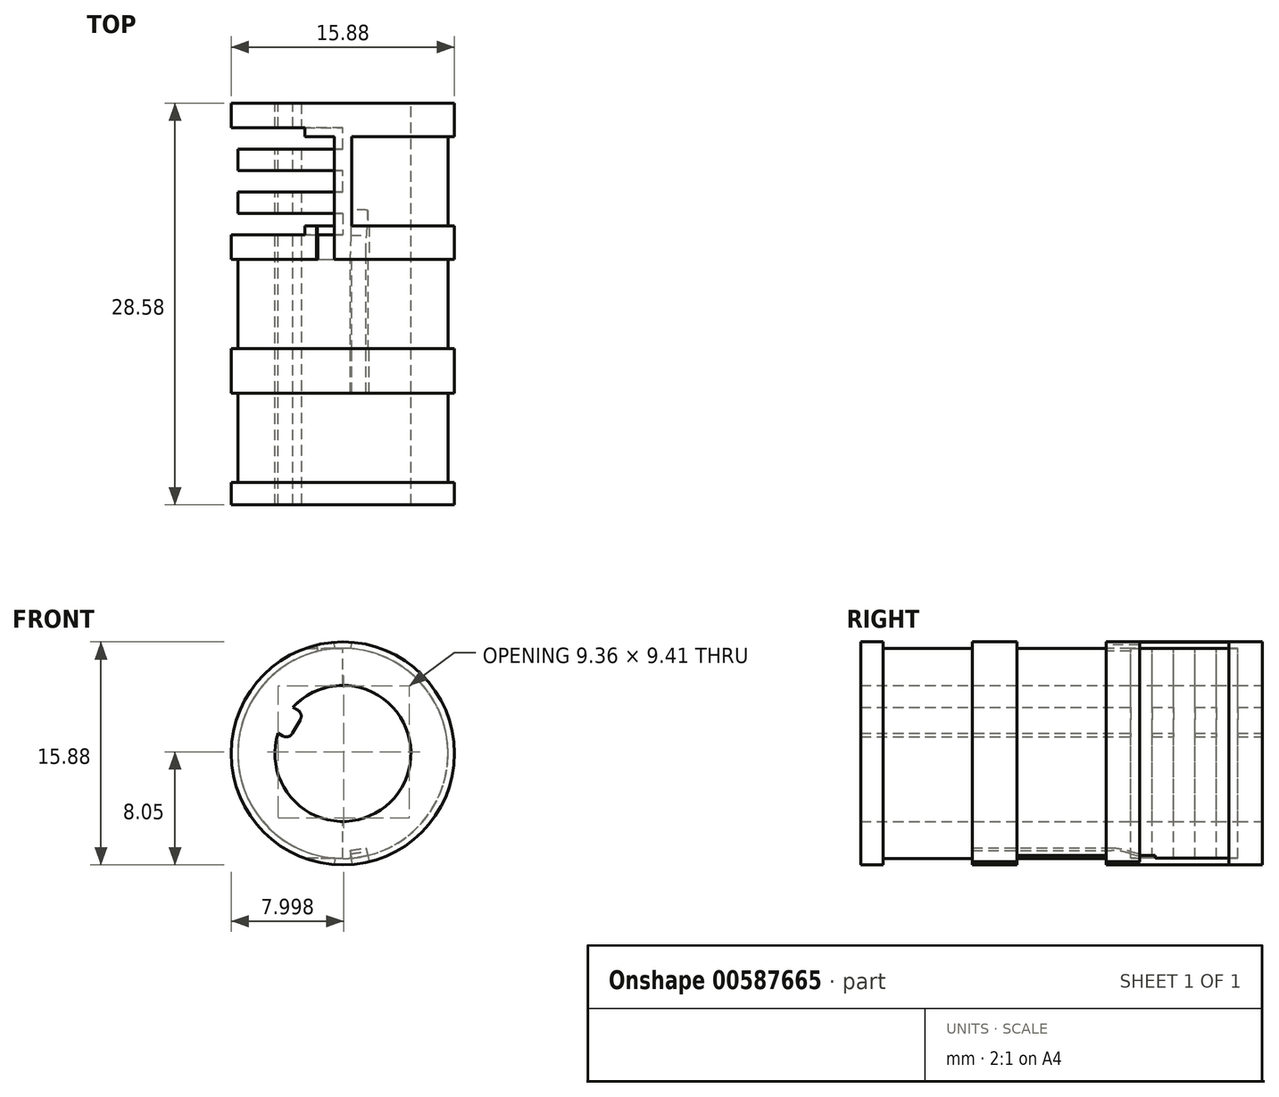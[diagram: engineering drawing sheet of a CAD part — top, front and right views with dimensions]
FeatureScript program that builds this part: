
annotation { "Feature Type Name" : "Feature", "Feature Type Description" : "" }
export const myFeature = defineFeature(function(context is Context, id is Id, definition is map)
    precondition{}
    {
        {
            var Q0;
            Q0=qCreatedBy(makeId("Front.planeOp"),FACE);
            var sketch = newSketch(context, id + "F0", { "sketchPlane" : qUnion([Q0])});
            skCircle(sketch, "E0", {"center": v(0, 0) * mm, "radius": 7.94 * mm});
            skCircle(sketch, "E1", {"center": v(0, 0) * mm, "radius": 4.84 * mm});
            skSolve(sketch);
        }
        {
            var Q0;
            Q0 = qSketchRegion(id + "F0", true);
            extrude(context, id + "F1", {"entities" : qUnion([Q0]), "endBound" : BoundingType.SYMMETRIC, "depth" : 11.1 * mm, "offsetDistance" : 25.4 * mm});
        }
        {
            var Q0;
            Q0=qCreatedBy(makeId("Front.planeOp"),FACE);
            var sketch = newSketch(context, id + "F2", { "sketchPlane" : qUnion([Q0])});
            skCircle(sketch, "E2.0", {"center": v(0, 0) * mm, "radius": 7.94 * mm, "construction": true});
            skLineSegment(sketch, "E3", {"start": v(0, 0) * mm, "end": v(0, 7.94) * mm, "construction": true});
            skLineSegment(sketch, "E4", {"start": v(0, 0) * mm, "end": v(0, -7.94) * mm, "construction": true});
            skLineSegment(sketch, "E5", {"start": v(0, 0) * mm, "end": v(-0.62, 7.91) * mm});
            skLineSegment(sketch, "E6", {"start": v(0, 0) * mm, "end": v(0.62, 7.91) * mm});
            skLineSegment(sketch, "E7", {"start": v(-0.62, 7.91) * mm, "end": v(0.62, 7.91) * mm, "construction": true});
            skLineSegment(sketch, "E8", {"start": v(0, 0) * mm, "end": v(0.62, -7.91) * mm});
            skLineSegment(sketch, "E9", {"start": v(0, 0) * mm, "end": v(-0.62, -7.91) * mm});
            skCircle(sketch, "E10", {"center": v(0, 0) * mm, "radius": 7.48 * mm});
            skCircle(sketch, "E11", {"center": v(0, 0) * mm, "radius": 8.45 * mm});
            skLineSegment(sketch, "E12", {"start": v(-0.62, 7.91) * mm, "end": v(-0.66, 8.42) * mm});
            skLineSegment(sketch, "E13", {"start": v(0.62, 7.91) * mm, "end": v(0.66, 8.42) * mm});
            skLineSegment(sketch, "E14", {"start": v(0.62, -7.91) * mm, "end": v(0.66, -8.42) * mm});
            skLineSegment(sketch, "E15", {"start": v(-0.62, -7.91) * mm, "end": v(-0.66, -8.42) * mm});
            skSolve(sketch);
        }
        {
            var Q0;
            {var subQ5=sQuery(id+"F2.wireOp",EDGE,"E13");Q0=makeQuery(id+"F2.imprint","IMPRINT",FACE,{"disambiguationData":[TD([[makeQuery(id+"F2.imprint","IMPRINT",EDGE,{"derivedFrom":subQ5}),-1.0]])]});}
            var Q1;
            {var subQ0=sQuery(id+"F2.wireOp",EDGE,"E12");Q1=makeQuery(id+"F2.imprint","IMPRINT",FACE,{"disambiguationData":[TD([[makeQuery(id+"F2.imprint","IMPRINT",EDGE,{"derivedFrom":subQ0}),1.0]])]});}
            extrude(context, id + "F3", {"entities" : qUnion([Q0, Q1]), "operationType" : NewBodyOperationType.REMOVE, "endBound" : BoundingType.SYMMETRIC, "oppositeDirection" : true, "depth" : 6.35 * mm, "offsetDistance" : 25.4 * mm});
        }
        {
            var Q0;
            Q0=qCreatedBy(makeId("Front.planeOp"),FACE);
            var sketch = newSketch(context, id + "F4", { "sketchPlane" : qUnion([Q0])});
            skLineSegment(sketch, "E16", {"start": v(0, 0) * mm, "end": v(-4.2, 2.42) * mm, "construction": true});
            skArc(sketch, "E17.0", {"start": v(-3.55, 3.28) * mm, "mid": v(-4.2, 2.42) * mm, "end": v(-4.62, 1.44) * mm});
            skLineSegment(sketch, "E18", {"start": v(-3.31, 1.91) * mm, "end": v(-3.84, 0.99) * mm});
            skLineSegment(sketch, "E19", {"start": v(-3.31, 1.91) * mm, "end": v(-2.78, 2.84) * mm});
            skLineSegment(sketch, "E20", {"start": v(-2.78, 2.84) * mm, "end": v(-3.55, 3.28) * mm});
            skLineSegment(sketch, "E21", {"start": v(-3.84, 0.99) * mm, "end": v(-4.62, 1.44) * mm});
            skLineSegment(sketch, "E22", {"start": v(0, 0) * mm, "end": v(0, -4.84) * mm, "construction": true});
            skSolve(sketch);
        }
        {
            var Q0;
            Q0=makeQuery(id+"F4.imprint","IMPRINT",FACE,{"disambiguationData":[TD([[makeQuery(id+"F4.imprint","IMPRINT",EDGE,{"derivedFrom":sQuery(id+"F4.wireOp",EDGE,"E17.0")}),1.0]])]});
            extrude(context, id + "F5", {"entities" : qUnion([Q0]), "operationType" : NewBodyOperationType.ADD, "endBound" : BoundingType.SYMMETRIC, "depth" : 11.1 * mm, "offsetDistance" : 25.4 * mm});
        }
        {
            var Q0;
            Q0=makeQuery(id+"F5.opExtrude","SWEPT_EDGE",EDGE,{"disambiguationData":[OSD([sQuery(id+"F4.wireOp",EDGE,"E19"),sQuery(id+"F4.wireOp",EDGE,"E20")])]});
            var Q1;
            Q1=makeQuery(id+"F5.opExtrude","SWEPT_EDGE",EDGE,{"disambiguationData":[OSD([sQuery(id+"F4.wireOp",EDGE,"E18"),sQuery(id+"F4.wireOp",EDGE,"E21")])]});
            fillet(context, id + "F6", {"entities" : qUnion([Q0, Q1]), "radius" : 0.5 * mm, "tangentPropagation" : true, "allowEdgeOverflow" : false});
        }
        {
            var Q0;
            Q0=qCreatedBy(makeId("Right.planeOp"),FACE);
            var sketch = newSketch(context, id + "F7", { "sketchPlane" : qUnion([Q0])});
            skLineSegment(sketch, "E23.bottom", {"start": v(3.81, -7.46) * mm, "end": v(2.29, -7.46) * mm});
            skLineSegment(sketch, "E23.top", {"start": v(3.8, 7.46) * mm, "end": v(2.29, 7.46) * mm});
            skLineSegment(sketch, "E23.left", {"start": v(3.81, -7.46) * mm, "end": v(3.8, 7.46) * mm});
            skLineSegment(sketch, "E23.right", {"start": v(2.29, -7.46) * mm, "end": v(2.29, 7.46) * mm});
            skLineSegment(sketch, "E24.bottom", {"start": v(0.76, -7.46) * mm, "end": v(-0.76, -7.46) * mm});
            skLineSegment(sketch, "E24.top", {"start": v(0.76, 7.46) * mm, "end": v(-0.76, 7.46) * mm});
            skLineSegment(sketch, "E24.left", {"start": v(0.76, -7.46) * mm, "end": v(0.76, 7.46) * mm});
            skLineSegment(sketch, "E24.right", {"start": v(-0.76, -7.46) * mm, "end": v(-0.76, 7.46) * mm});
            skLineSegment(sketch, "E25.bottom", {"start": v(-2.29, -7.46) * mm, "end": v(-3.8, -7.46) * mm});
            skLineSegment(sketch, "E25.top", {"start": v(-2.29, 7.46) * mm, "end": v(-3.81, 7.46) * mm});
            skLineSegment(sketch, "E25.left", {"start": v(-2.29, -7.46) * mm, "end": v(-2.29, 7.46) * mm});
            skLineSegment(sketch, "E25.right", {"start": v(-3.8, -7.46) * mm, "end": v(-3.81, 7.46) * mm});
            skLineSegment(sketch, "E26", {"start": v(0, 0) * mm, "end": v(0.76, 0) * mm, "construction": true});
            skLineSegment(sketch, "E27", {"start": v(0.76, 0) * mm, "end": v(2.29, 0) * mm, "construction": true});
            skLineSegment(sketch, "E28", {"start": v(0, 0) * mm, "end": v(-0.76, 0) * mm, "construction": true});
            skLineSegment(sketch, "E29", {"start": v(-0.76, 0) * mm, "end": v(-2.29, 0) * mm, "construction": true});
            skSolve(sketch);
        }
        {
            var Q0;
            Q0 = qSketchRegion(id + "F7", true);
            extrude(context, id + "F8", {"entities" : qUnion([Q0]), "operationType" : NewBodyOperationType.REMOVE, "oppositeDirection" : true, "depth" : 25.4 * mm, "offsetDistance" : 25.4 * mm});
        }
        {
            var Q0;
            Q0=makeQuery(id+"F5.boolean.opBoolean","MERGE",FACE,{"derivedFrom":[makeQuery(id+"F1.opExtrude","CAP_FACE",FACE,{"disambiguationData":[OSD([sQuery(id+"F0.wireOp",EDGE,"E0"),sQuery(id+"F0.wireOp",EDGE,"E1")])],"isStart":false}),makeQuery(id+"F5.opExtrude","CAP_FACE",FACE,{"disambiguationData":[OSD([sQuery(id+"F4.wireOp",EDGE,"E17.0"),sQuery(id+"F4.wireOp",EDGE,"E18"),sQuery(id+"F4.wireOp",EDGE,"E19"),sQuery(id+"F4.wireOp",EDGE,"E20"),sQuery(id+"F4.wireOp",EDGE,"E21")])],"isStart":false})]});
            var sketch = newSketch(context, id + "F9", { "sketchPlane" : qUnion([Q0])});
            skArc(sketch, "E30.0", {"start": v(-4.62, 1.44) * mm, "mid": v(4.2, -2.42) * mm, "end": v(-3.55, 3.28) * mm});
            skLineSegment(sketch, "E30.1", {"start": v(-4.28, 1.24) * mm, "end": v(-4.62, 1.44) * mm});
            skArc(sketch, "E30.2", {"start": v(-4.28, 1.24) * mm, "mid": v(-3.9, 1.2) * mm, "end": v(-3.59, 1.43) * mm});
            skLineSegment(sketch, "E30.3", {"start": v(-3.03, 2.4) * mm, "end": v(-3.59, 1.43) * mm});
            skArc(sketch, "E30.4", {"start": v(-3.03, 2.4) * mm, "mid": v(-2.98, 2.78) * mm, "end": v(-3.22, 3.09) * mm});
            skLineSegment(sketch, "E30.5", {"start": v(-3.22, 3.09) * mm, "end": v(-3.55, 3.28) * mm});
            skArc(sketch, "E31.0", {"start": v(0.59, -7.46) * mm, "mid": v(7.48, 0) * mm, "end": v(0.59, 7.46) * mm, "construction": true});
            skCircle(sketch, "E32", {"center": v(0, 0) * mm, "radius": 7.48 * mm});
            skSolve(sketch);
        }
        {
            var Q0;
            Q0 = qSketchRegion(id + "F9", true);
            extrude(context, id + "F10", {"entities" : qUnion([Q0]), "operationType" : NewBodyOperationType.ADD, "depth" : 6.35 * mm, "offsetDistance" : 25.4 * mm});
        }
        {
            var Q0;
            Q0=makeQuery(id+"F10.opExtrude","CAP_FACE",FACE,{"disambiguationData":[OSD([sQuery(id+"F9.wireOp",EDGE,"E30.0"),sQuery(id+"F9.wireOp",EDGE,"E30.1"),sQuery(id+"F9.wireOp",EDGE,"E30.2"),sQuery(id+"F9.wireOp",EDGE,"E30.3"),sQuery(id+"F9.wireOp",EDGE,"E30.4"),sQuery(id+"F9.wireOp",EDGE,"E30.5"),sQuery(id+"F9.wireOp",EDGE,"E32")])],"isStart":false});
            var sketch = newSketch(context, id + "F11", { "sketchPlane" : qUnion([Q0])});
            skCircle(sketch, "E33.0", {"center": v(0, 0) * mm, "radius": 7.94 * mm});
            skArc(sketch, "E34.0", {"start": v(-4.62, 1.44) * mm, "mid": v(4.2, -2.42) * mm, "end": v(-3.55, 3.28) * mm});
            skLineSegment(sketch, "E34.1", {"start": v(-4.28, 1.24) * mm, "end": v(-4.62, 1.44) * mm});
            skArc(sketch, "E34.2", {"start": v(-4.28, 1.24) * mm, "mid": v(-3.9, 1.2) * mm, "end": v(-3.59, 1.43) * mm});
            skLineSegment(sketch, "E34.3", {"start": v(-3.03, 2.4) * mm, "end": v(-3.59, 1.43) * mm});
            skArc(sketch, "E34.4", {"start": v(-3.03, 2.4) * mm, "mid": v(-2.98, 2.78) * mm, "end": v(-3.22, 3.09) * mm});
            skLineSegment(sketch, "E34.5", {"start": v(-3.22, 3.09) * mm, "end": v(-3.55, 3.28) * mm});
            skSolve(sketch);
        }
        {
            var Q0;
            Q0 = qSketchRegion(id + "F11", true);
            extrude(context, id + "F12", {"entities" : qUnion([Q0]), "operationType" : NewBodyOperationType.ADD, "depth" : 3.17 * mm, "offsetDistance" : 25.4 * mm});
        }
        {
            var Q0;
            Q0=makeQuery(id+"F12.opExtrude","CAP_FACE",FACE,{"disambiguationData":[OSD([sQuery(id+"F11.wireOp",EDGE,"E33.0"),sQuery(id+"F11.wireOp",EDGE,"E34.0"),sQuery(id+"F11.wireOp",EDGE,"E34.1"),sQuery(id+"F11.wireOp",EDGE,"E34.2"),sQuery(id+"F11.wireOp",EDGE,"E34.3"),sQuery(id+"F11.wireOp",EDGE,"E34.4"),sQuery(id+"F11.wireOp",EDGE,"E34.5")])],"isStart":false});
            var sketch = newSketch(context, id + "F13", { "sketchPlane" : qUnion([Q0])});
            skArc(sketch, "E35.0", {"start": v(-4.62, 1.44) * mm, "mid": v(4.2, -2.42) * mm, "end": v(-3.55, 3.28) * mm});
            skLineSegment(sketch, "E35.1", {"start": v(-4.28, 1.24) * mm, "end": v(-4.62, 1.44) * mm});
            skArc(sketch, "E35.2", {"start": v(-4.28, 1.24) * mm, "mid": v(-3.9, 1.2) * mm, "end": v(-3.59, 1.43) * mm});
            skLineSegment(sketch, "E35.3", {"start": v(-3.03, 2.4) * mm, "end": v(-3.59, 1.43) * mm});
            skArc(sketch, "E35.4", {"start": v(-3.03, 2.4) * mm, "mid": v(-2.98, 2.78) * mm, "end": v(-3.22, 3.09) * mm});
            skLineSegment(sketch, "E35.5", {"start": v(-3.22, 3.09) * mm, "end": v(-3.55, 3.28) * mm});
            skArc(sketch, "E35.6", {"start": v(0.59, -7.46) * mm, "mid": v(7.48, 0) * mm, "end": v(0.59, 7.46) * mm});
            skCircle(sketch, "E35.7", {"center": v(0, 0) * mm, "radius": 7.48 * mm});
            skSolve(sketch);
        }
        {
            var Q0;
            Q0 = qSketchRegion(id + "F13", true);
            extrude(context, id + "F14", {"entities" : qUnion([Q0]), "operationType" : NewBodyOperationType.ADD, "depth" : 6.35 * mm, "offsetDistance" : 25.4 * mm});
        }
        {
            var Q0;
            Q0=makeQuery(id+"F14.opExtrude","CAP_FACE",FACE,{"disambiguationData":[OSD([sQuery(id+"F13.wireOp",EDGE,"E35.0"),sQuery(id+"F13.wireOp",EDGE,"E35.1"),sQuery(id+"F13.wireOp",EDGE,"E35.2"),sQuery(id+"F13.wireOp",EDGE,"E35.3"),sQuery(id+"F13.wireOp",EDGE,"E35.4"),sQuery(id+"F13.wireOp",EDGE,"E35.5"),sQuery(id+"F13.wireOp",EDGE,"E35.7")])],"isStart":false});
            var sketch = newSketch(context, id + "F15", { "sketchPlane" : qUnion([Q0])});
            skCircle(sketch, "E36.0", {"center": v(0, 0) * mm, "radius": 7.94 * mm});
            skArc(sketch, "E36.1", {"start": v(-4.62, 1.44) * mm, "mid": v(4.2, -2.42) * mm, "end": v(-3.55, 3.28) * mm});
            skLineSegment(sketch, "E36.2", {"start": v(-4.28, 1.24) * mm, "end": v(-4.62, 1.44) * mm});
            skArc(sketch, "E36.3", {"start": v(-4.28, 1.24) * mm, "mid": v(-3.9, 1.2) * mm, "end": v(-3.59, 1.43) * mm});
            skLineSegment(sketch, "E36.4", {"start": v(-3.03, 2.4) * mm, "end": v(-3.59, 1.43) * mm});
            skArc(sketch, "E36.5", {"start": v(-3.03, 2.4) * mm, "mid": v(-2.98, 2.78) * mm, "end": v(-3.22, 3.09) * mm});
            skLineSegment(sketch, "E36.6", {"start": v(-3.22, 3.09) * mm, "end": v(-3.55, 3.28) * mm});
            skSolve(sketch);
        }
        {
            var Q0;
            Q0 = qSketchRegion(id + "F15", true);
            extrude(context, id + "F16", {"entities" : qUnion([Q0]), "operationType" : NewBodyOperationType.ADD, "depth" : 1.59 * mm, "offsetDistance" : 25.4 * mm});
        }
        {
            var Q0;
            Q0=makeQuery(id+"F5.boolean.opBoolean","MERGE",FACE,{"derivedFrom":[makeQuery(id+"F1.opExtrude","CAP_FACE",FACE,{"disambiguationData":[OSD([sQuery(id+"F0.wireOp",EDGE,"E0"),sQuery(id+"F0.wireOp",EDGE,"E1")])],"isStart":false}),makeQuery(id+"F5.opExtrude","CAP_FACE",FACE,{"disambiguationData":[OSD([sQuery(id+"F4.wireOp",EDGE,"E17.0"),sQuery(id+"F4.wireOp",EDGE,"E18"),sQuery(id+"F4.wireOp",EDGE,"E19"),sQuery(id+"F4.wireOp",EDGE,"E20"),sQuery(id+"F4.wireOp",EDGE,"E21")])],"isStart":false})]});
            var sketch = newSketch(context, id + "F17", { "sketchPlane" : qUnion([Q0])});
            skLineSegment(sketch, "E37.0", {"start": v(-0.59, 7.46) * mm, "end": v(-0.62, 7.91) * mm});
            skArc(sketch, "E37.1", {"start": v(-0.62, 7.91) * mm, "mid": v(-1.25, 7.84) * mm, "end": v(-1.88, 7.71) * mm});
            skArc(sketch, "E37.2", {"start": v(-0.59, 7.46) * mm, "mid": v(-1.18, 7.39) * mm, "end": v(-1.77, 7.27) * mm});
            skLineSegment(sketch, "E38", {"start": v(-1.77, 7.27) * mm, "end": v(-1.88, 7.71) * mm});
            skLineSegment(sketch, "E39", {"start": v(-1.77, 7.27) * mm, "end": v(0, 0) * mm, "construction": true});
            skPoint(sketch, "E40.orphan", {"position": v(-2.72, 7.46) * mm});
            skPoint(sketch, "E41.orphan", {"position": v(-0.59, -7.46) * mm});
            skLineSegment(sketch, "E42", {"start": v(0, 0) * mm, "end": v(1.77, -7.27) * mm, "construction": true});
            skArc(sketch, "E43.0", {"start": v(0.59, -7.46) * mm, "mid": v(1.18, -7.39) * mm, "end": v(1.77, -7.27) * mm});
            skArc(sketch, "E44.0", {"start": v(0.62, -7.91) * mm, "mid": v(1.25, -7.84) * mm, "end": v(1.88, -7.71) * mm});
            skLineSegment(sketch, "E45", {"start": v(1.77, -7.27) * mm, "end": v(1.88, -7.71) * mm});
            skLineSegment(sketch, "E46", {"start": v(0.59, -7.46) * mm, "end": v(0.62, -7.91) * mm});
            skPoint(sketch, "E47.orphan", {"position": v(0.59, 7.46) * mm});
            skPoint(sketch, "E48.orphan", {"position": v(0.62, 7.91) * mm});
            skSolve(sketch);
        }
        {
            var Q0;
            Q0 = qSketchRegion(id + "F17", true);
            var Q1;
            Q1=makeQuery(id+"F3.boolean.opBoolean","COPY",FACE,{"derivedFrom":makeQuery(id+"F3.opExtrude","CAP_FACE",FACE,{"disambiguationData":[OSD([sQuery(id+"F2.wireOp",EDGE,"E5"),sQuery(id+"F2.wireOp",EDGE,"E9"),sQuery(id+"F2.wireOp",EDGE,"E10"),sQuery(id+"F2.wireOp",EDGE,"E11"),sQuery(id+"F2.wireOp",EDGE,"E12"),sQuery(id+"F2.wireOp",EDGE,"E15")])],"isStart":true})});
            extrude(context, id + "F18", {"entities" : qUnion([Q0]), "operationType" : NewBodyOperationType.REMOVE, "endBound" : BoundingType.UP_TO_SURFACE, "oppositeDirection" : true, "depth" : 25.4 * mm, "endBoundEntityFace" : qUnion([Q1]), "offsetDistance" : 25.4 * mm});
        }
        {
            var Q0;
            Q0=makeQuery(id+"F12.opExtrude","CAP_FACE",FACE,{"disambiguationData":[OSD([sQuery(id+"F11.wireOp",EDGE,"E33.0"),sQuery(id+"F11.wireOp",EDGE,"E34.0"),sQuery(id+"F11.wireOp",EDGE,"E34.1"),sQuery(id+"F11.wireOp",EDGE,"E34.2"),sQuery(id+"F11.wireOp",EDGE,"E34.3"),sQuery(id+"F11.wireOp",EDGE,"E34.4"),sQuery(id+"F11.wireOp",EDGE,"E34.5")])],"isStart":true});
            var sketch = newSketch(context, id + "F19", { "sketchPlane" : qUnion([Q0])});
            skPoint(sketch, "E49.5", {"position": v(2.72, 7.46) * mm});
            skPoint(sketch, "E49.6", {"position": v(0.59, -7.46) * mm});
            skArc(sketch, "E49.8", {"start": v(-0.59, -7.46) * mm, "mid": v(-1.18, -7.39) * mm, "end": v(-1.77, -7.27) * mm});
            skArc(sketch, "E49.9", {"start": v(-0.62, -7.91) * mm, "mid": v(-1.25, -7.84) * mm, "end": v(-1.88, -7.71) * mm});
            skLineSegment(sketch, "E49.10", {"start": v(-1.77, -7.27) * mm, "end": v(-1.88, -7.71) * mm});
            skLineSegment(sketch, "E49.11", {"start": v(-0.59, -7.46) * mm, "end": v(-0.62, -7.91) * mm});
            skPoint(sketch, "E49.12", {"position": v(-0.59, 7.46) * mm});
            skPoint(sketch, "E49.13", {"position": v(-0.62, 7.91) * mm});
            skSolve(sketch);
        }
        {
            var Q0;
            Q0 = qSketchRegion(id + "F19", true);
            var Q1;
            Q1=makeQuery(id+"F12.opExtrude","CAP_FACE",FACE,{"disambiguationData":[OSD([sQuery(id+"F11.wireOp",EDGE,"E33.0"),sQuery(id+"F11.wireOp",EDGE,"E34.0"),sQuery(id+"F11.wireOp",EDGE,"E34.1"),sQuery(id+"F11.wireOp",EDGE,"E34.2"),sQuery(id+"F11.wireOp",EDGE,"E34.3"),sQuery(id+"F11.wireOp",EDGE,"E34.4"),sQuery(id+"F11.wireOp",EDGE,"E34.5")])],"isStart":false});
            extrude(context, id + "F20", {"entities" : qUnion([Q0]), "operationType" : NewBodyOperationType.REMOVE, "endBound" : BoundingType.UP_TO_SURFACE, "oppositeDirection" : true, "depth" : 25.4 * mm, "endBoundEntityFace" : qUnion([Q1]), "offsetDistance" : 25.4 * mm});
        }
        {
            var Q0;
            Q0=makeQuery(id+"F3.boolean.opBoolean","COPY",FACE,{"derivedFrom":makeQuery(id+"F3.opExtrude","CAP_FACE",FACE,{"disambiguationData":[OSD([sQuery(id+"F2.wireOp",EDGE,"E6"),sQuery(id+"F2.wireOp",EDGE,"E8"),sQuery(id+"F2.wireOp",EDGE,"E10"),sQuery(id+"F2.wireOp",EDGE,"E11"),sQuery(id+"F2.wireOp",EDGE,"E13"),sQuery(id+"F2.wireOp",EDGE,"E14")])],"isStart":true})});
            var sketch = newSketch(context, id + "F21", { "sketchPlane" : qUnion([Q0])});
            skLineSegment(sketch, "E50.0", {"start": v(-1.88, -7.71) * mm, "end": v(-1.77, -7.27) * mm});
            skLineSegment(sketch, "E51.0", {"start": v(-0.59, -7.46) * mm, "end": v(-0.62, -7.91) * mm});
            skLineSegment(sketch, "E52", {"start": v(-0.59, -7.46) * mm, "end": v(-0.54, -6.9) * mm});
            skLineSegment(sketch, "E53", {"start": v(-0.54, -6.9) * mm, "end": v(-1.64, -6.73) * mm});
            skLineSegment(sketch, "E54", {"start": v(-1.64, -6.73) * mm, "end": v(-1.77, -7.27) * mm});
            skLineSegment(sketch, "E55", {"start": v(-0.62, -7.91) * mm, "end": v(-1.88, -7.71) * mm});
            skSolve(sketch);
        }
        {
            var Q0;
            Q0 = qSketchRegion(id + "F21", true);
            var Q1;
            Q1=makeQuery(id+"F12.opExtrude","CAP_FACE",FACE,{"disambiguationData":[OSD([sQuery(id+"F11.wireOp",EDGE,"E33.0"),sQuery(id+"F11.wireOp",EDGE,"E34.0"),sQuery(id+"F11.wireOp",EDGE,"E34.1"),sQuery(id+"F11.wireOp",EDGE,"E34.2"),sQuery(id+"F11.wireOp",EDGE,"E34.3"),sQuery(id+"F11.wireOp",EDGE,"E34.4"),sQuery(id+"F11.wireOp",EDGE,"E34.5")])],"isStart":false});
            extrude(context, id + "F22", {"entities" : qUnion([Q0]), "operationType" : NewBodyOperationType.REMOVE, "endBound" : BoundingType.UP_TO_SURFACE, "oppositeDirection" : true, "depth" : 25.4 * mm, "endBoundEntityFace" : qUnion([Q1]), "offsetDistance" : 25.4 * mm});
        }
        {
            var Q0;
            Q0=makeQuery(id+"F22.boolean.opBoolean","COPY",EDGE,{"derivedFrom":makeQuery(id+"F22.opExtrude","CAP_EDGE",EDGE,{"disambiguationData":[OSD([sQuery(id+"F21.wireOp",EDGE,"E53")])],"isStart":true})});
            var Q1;
            Q1=makeQuery(id+"F22.boolean.opBoolean","COPY",EDGE,{"derivedFrom":makeQuery(id+"F22.opExtrude","TWEAK_EDGE",EDGE,{"derivedFrom":[makeQuery(id+"F12.opExtrude","CAP_FACE",FACE,{"disambiguationData":[OSD([sQuery(id+"F11.wireOp",EDGE,"E33.0"),sQuery(id+"F11.wireOp",EDGE,"E34.0"),sQuery(id+"F11.wireOp",EDGE,"E34.1"),sQuery(id+"F11.wireOp",EDGE,"E34.2"),sQuery(id+"F11.wireOp",EDGE,"E34.3"),sQuery(id+"F11.wireOp",EDGE,"E34.4"),sQuery(id+"F11.wireOp",EDGE,"E34.5")])],"isStart":false}),makeQuery(id+"F21.imprint","IMPRINT",EDGE,{"derivedFrom":sQuery(id+"F21.wireOp",EDGE,"E53")})]})});
            fillet(context, id + "F23", {"entities" : qUnion([Q0, Q1]), "radius" : 3.8 * mm, "tangentPropagation" : true, "allowEdgeOverflow" : false});
        }
        {
            var Q0;
            {var subQ2=sQuery(id+"F21.wireOp",EDGE,"E53");var subQ6=sQuery(id+"F2.wireOp",EDGE,"E13");var subQ8=sQuery(id+"F2.wireOp",EDGE,"E10");var subQ10=sQuery(id+"F2.wireOp",EDGE,"E6");Q0=makeQuery(id+"F23.opFillet","BLEND_EDGE",EDGE,{"blendedFrom":[makeQuery(id+"F22.boolean.opBoolean","COPY",EDGE,{"derivedFrom":makeQuery(id+"F22.opExtrude","CAP_EDGE",EDGE,{"disambiguationData":[OSD([subQ2])],"isStart":true})}),makeQuery(id+"F22.boolean.opBoolean","SPLIT",FACE,{"disambiguationData":[TD([makeQuery(id+"F3.boolean.opBoolean","COPY",FACE,{"derivedFrom":makeQuery(id+"F3.opExtrude","SWEPT_FACE",FACE,{"disambiguationData":[OSD([subQ10,subQ6])]})})])],"derivedFrom":makeQuery(id+"F20.boolean.opBoolean","MERGE",FACE,{"derivedFrom":[makeQuery(id+"F14.opExtrude","SWEPT_FACE",FACE,{"disambiguationData":[OSD([sQuery(id+"F13.wireOp",EDGE,"E35.7")])]}),makeQuery(id+"F18.boolean.opBoolean","MERGE",FACE,{"derivedFrom":[makeQuery(id+"F3.boolean.opBoolean","COPY",FACE,{"derivedFrom":makeQuery(id+"F3.opExtrude","SWEPT_FACE",FACE,{"disambiguationData":[OSD([subQ8]),TDD([makeQuery(id+"F2.imprint","IMPRINT",EDGE,{"disambiguationData":[TD([[makeQuery(id+"F2.imprint","INTERSECT",VERTEX,{"derivedFrom":[sQuery(id+"F2.wireOp",EDGE,"E5"),subQ8]}),-1.0]])],"derivedFrom":subQ8})])]})}),makeQuery(id+"F3.boolean.opBoolean","COPY",FACE,{"derivedFrom":makeQuery(id+"F3.opExtrude","SWEPT_FACE",FACE,{"disambiguationData":[OSD([subQ8]),TDD([makeQuery(id+"F2.imprint","IMPRINT",EDGE,{"disambiguationData":[TD([[makeQuery(id+"F2.imprint","INTERSECT",VERTEX,{"derivedFrom":[subQ10,subQ8]}),1.0]])],"derivedFrom":subQ8})])]})}),makeQuery(id+"F10.opExtrude","SWEPT_FACE",FACE,{"disambiguationData":[OSD([sQuery(id+"F9.wireOp",EDGE,"E32")])]}),makeQuery(id+"F18.opExtrude","SWEPT_FACE",FACE,{"disambiguationData":[OSD([sQuery(id+"F17.wireOp",EDGE,"E37.2")])]}),makeQuery(id+"F18.opExtrude","SWEPT_FACE",FACE,{"disambiguationData":[OSD([sQuery(id+"F17.wireOp",EDGE,"E43.0")])]})]}),makeQuery(id+"F20.opExtrude","SWEPT_FACE",FACE,{"disambiguationData":[OSD([sQuery(id+"F19.wireOp",EDGE,"E49.8")])]})]})})],"blendedInto":[makeQuery(id+"F22.boolean.opBoolean","SPLIT",FACE,{"disambiguationData":[TD([makeQuery(id+"F3.boolean.opBoolean","COPY",FACE,{"derivedFrom":makeQuery(id+"F3.opExtrude","SWEPT_FACE",FACE,{"disambiguationData":[OSD([subQ10,subQ6])]})})])],"derivedFrom":makeQuery(id+"F20.boolean.opBoolean","MERGE",FACE,{"derivedFrom":[makeQuery(id+"F14.opExtrude","SWEPT_FACE",FACE,{"disambiguationData":[OSD([sQuery(id+"F13.wireOp",EDGE,"E35.7")])]}),makeQuery(id+"F18.boolean.opBoolean","MERGE",FACE,{"derivedFrom":[makeQuery(id+"F3.boolean.opBoolean","COPY",FACE,{"derivedFrom":makeQuery(id+"F3.opExtrude","SWEPT_FACE",FACE,{"disambiguationData":[OSD([subQ8]),TDD([makeQuery(id+"F2.imprint","IMPRINT",EDGE,{"disambiguationData":[TD([[makeQuery(id+"F2.imprint","INTERSECT",VERTEX,{"derivedFrom":[sQuery(id+"F2.wireOp",EDGE,"E5"),subQ8]}),-1.0]])],"derivedFrom":subQ8})])]})}),makeQuery(id+"F3.boolean.opBoolean","COPY",FACE,{"derivedFrom":makeQuery(id+"F3.opExtrude","SWEPT_FACE",FACE,{"disambiguationData":[OSD([subQ8]),TDD([makeQuery(id+"F2.imprint","IMPRINT",EDGE,{"disambiguationData":[TD([[makeQuery(id+"F2.imprint","INTERSECT",VERTEX,{"derivedFrom":[subQ10,subQ8]}),1.0]])],"derivedFrom":subQ8})])]})}),makeQuery(id+"F10.opExtrude","SWEPT_FACE",FACE,{"disambiguationData":[OSD([sQuery(id+"F9.wireOp",EDGE,"E32")])]}),makeQuery(id+"F18.opExtrude","SWEPT_FACE",FACE,{"disambiguationData":[OSD([sQuery(id+"F17.wireOp",EDGE,"E37.2")])]}),makeQuery(id+"F18.opExtrude","SWEPT_FACE",FACE,{"disambiguationData":[OSD([sQuery(id+"F17.wireOp",EDGE,"E43.0")])]})]}),makeQuery(id+"F20.opExtrude","SWEPT_FACE",FACE,{"disambiguationData":[OSD([sQuery(id+"F19.wireOp",EDGE,"E49.8")])]})]})})]});}
            var Q1;
            {var subQ0=sQuery(id+"F11.wireOp",EDGE,"E34.5");var subQ1=sQuery(id+"F11.wireOp",EDGE,"E34.4");var subQ2=sQuery(id+"F11.wireOp",EDGE,"E34.3");var subQ3=sQuery(id+"F11.wireOp",EDGE,"E34.2");var subQ4=sQuery(id+"F11.wireOp",EDGE,"E34.1");var subQ5=sQuery(id+"F11.wireOp",EDGE,"E34.0");var subQ6=sQuery(id+"F11.wireOp",EDGE,"E33.0");var subQ7=makeQuery(id+"F12.opExtrude","CAP_FACE",FACE,{"disambiguationData":[OSD([subQ6,subQ5,subQ4,subQ3,subQ2,subQ1,subQ0])],"isStart":false});var subQ9=sQuery(id+"F2.wireOp",EDGE,"E10");Q1=makeQuery(id+"F23.opFillet","BLEND_EDGE",EDGE,{"blendedFrom":[makeQuery(id+"F22.boolean.opBoolean","COPY",EDGE,{"derivedFrom":makeQuery(id+"F22.opExtrude","TWEAK_EDGE",EDGE,{"derivedFrom":[subQ7,makeQuery(id+"F21.imprint","IMPRINT",EDGE,{"derivedFrom":sQuery(id+"F21.wireOp",EDGE,"E53")})]})}),makeQuery(id+"F22.boolean.opBoolean","SPLIT",FACE,{"disambiguationData":[TD([subQ7])],"derivedFrom":makeQuery(id+"F20.boolean.opBoolean","MERGE",FACE,{"derivedFrom":[makeQuery(id+"F14.opExtrude","SWEPT_FACE",FACE,{"disambiguationData":[OSD([sQuery(id+"F13.wireOp",EDGE,"E35.7")])]}),makeQuery(id+"F18.boolean.opBoolean","MERGE",FACE,{"derivedFrom":[makeQuery(id+"F3.boolean.opBoolean","COPY",FACE,{"derivedFrom":makeQuery(id+"F3.opExtrude","SWEPT_FACE",FACE,{"disambiguationData":[OSD([subQ9]),TDD([makeQuery(id+"F2.imprint","IMPRINT",EDGE,{"disambiguationData":[TD([[makeQuery(id+"F2.imprint","INTERSECT",VERTEX,{"derivedFrom":[sQuery(id+"F2.wireOp",EDGE,"E5"),subQ9]}),-1.0]])],"derivedFrom":subQ9})])]})}),makeQuery(id+"F3.boolean.opBoolean","COPY",FACE,{"derivedFrom":makeQuery(id+"F3.opExtrude","SWEPT_FACE",FACE,{"disambiguationData":[OSD([subQ9]),TDD([makeQuery(id+"F2.imprint","IMPRINT",EDGE,{"disambiguationData":[TD([[makeQuery(id+"F2.imprint","INTERSECT",VERTEX,{"derivedFrom":[sQuery(id+"F2.wireOp",EDGE,"E6"),subQ9]}),1.0]])],"derivedFrom":subQ9})])]})}),makeQuery(id+"F10.opExtrude","SWEPT_FACE",FACE,{"disambiguationData":[OSD([sQuery(id+"F9.wireOp",EDGE,"E32")])]}),makeQuery(id+"F18.opExtrude","SWEPT_FACE",FACE,{"disambiguationData":[OSD([sQuery(id+"F17.wireOp",EDGE,"E37.2")])]}),makeQuery(id+"F18.opExtrude","SWEPT_FACE",FACE,{"disambiguationData":[OSD([sQuery(id+"F17.wireOp",EDGE,"E43.0")])]})]}),makeQuery(id+"F20.opExtrude","SWEPT_FACE",FACE,{"disambiguationData":[OSD([sQuery(id+"F19.wireOp",EDGE,"E49.8")])]})]})})],"blendedInto":[makeQuery(id+"F22.boolean.opBoolean","SPLIT",FACE,{"disambiguationData":[TD([subQ7])],"derivedFrom":makeQuery(id+"F20.boolean.opBoolean","MERGE",FACE,{"derivedFrom":[makeQuery(id+"F14.opExtrude","SWEPT_FACE",FACE,{"disambiguationData":[OSD([sQuery(id+"F13.wireOp",EDGE,"E35.7")])]}),makeQuery(id+"F18.boolean.opBoolean","MERGE",FACE,{"derivedFrom":[makeQuery(id+"F3.boolean.opBoolean","COPY",FACE,{"derivedFrom":makeQuery(id+"F3.opExtrude","SWEPT_FACE",FACE,{"disambiguationData":[OSD([subQ9]),TDD([makeQuery(id+"F2.imprint","IMPRINT",EDGE,{"disambiguationData":[TD([[makeQuery(id+"F2.imprint","INTERSECT",VERTEX,{"derivedFrom":[sQuery(id+"F2.wireOp",EDGE,"E5"),subQ9]}),-1.0]])],"derivedFrom":subQ9})])]})}),makeQuery(id+"F3.boolean.opBoolean","COPY",FACE,{"derivedFrom":makeQuery(id+"F3.opExtrude","SWEPT_FACE",FACE,{"disambiguationData":[OSD([subQ9]),TDD([makeQuery(id+"F2.imprint","IMPRINT",EDGE,{"disambiguationData":[TD([[makeQuery(id+"F2.imprint","INTERSECT",VERTEX,{"derivedFrom":[sQuery(id+"F2.wireOp",EDGE,"E6"),subQ9]}),1.0]])],"derivedFrom":subQ9})])]})}),makeQuery(id+"F10.opExtrude","SWEPT_FACE",FACE,{"disambiguationData":[OSD([sQuery(id+"F9.wireOp",EDGE,"E32")])]}),makeQuery(id+"F18.opExtrude","SWEPT_FACE",FACE,{"disambiguationData":[OSD([sQuery(id+"F17.wireOp",EDGE,"E37.2")])]}),makeQuery(id+"F18.opExtrude","SWEPT_FACE",FACE,{"disambiguationData":[OSD([sQuery(id+"F17.wireOp",EDGE,"E43.0")])]})]}),makeQuery(id+"F20.opExtrude","SWEPT_FACE",FACE,{"disambiguationData":[OSD([sQuery(id+"F19.wireOp",EDGE,"E49.8")])]})]})})]});}
            fillet(context, id + "F24", {"entities" : qUnion([Q0, Q1]), "radius" : 5.08 * mm, "tangentPropagation" : true, "allowEdgeOverflow" : false});
        }
    });
